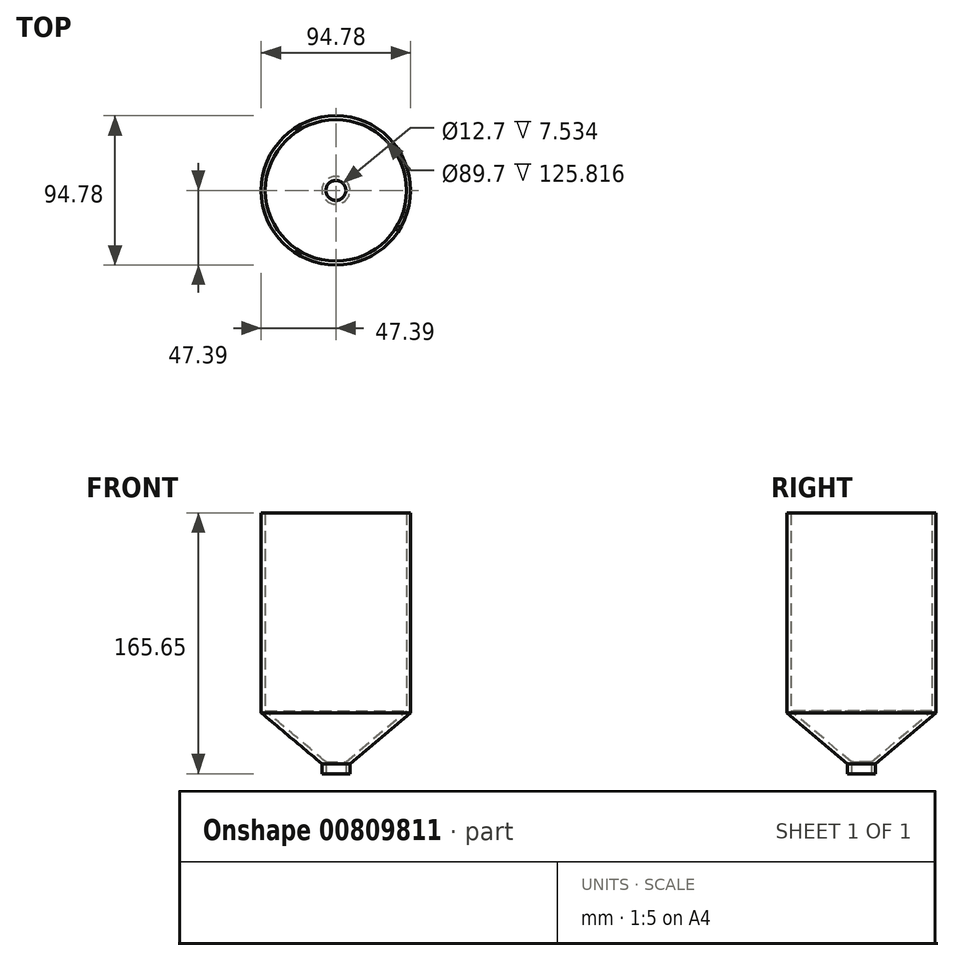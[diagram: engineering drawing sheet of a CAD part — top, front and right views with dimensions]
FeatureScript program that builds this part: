
annotation { "Feature Type Name" : "Feature", "Feature Type Description" : "" }
export const myFeature = defineFeature(function(context is Context, id is Id, definition is map)
    precondition{}
    {
        {
            var Q0;
            Q0=qCreatedBy(makeId("Right.planeOp"),FACE);
            var sketch = newSketch(context, id + "F0", { "sketchPlane" : qUnion([Q0])});
            skLineSegment(sketch, "E0", {"start": v(0, 0) * mm, "end": v(0, 23.87) * mm, "construction": true});
            skLineSegment(sketch, "E1", {"start": v(6.35, 0) * mm, "end": v(6.35, 7.53) * mm});
            skLineSegment(sketch, "E2", {"start": v(6.35, 7.53) * mm, "end": v(44.85, 39.84) * mm});
            skLineSegment(sketch, "E3", {"start": v(44.85, 39.84) * mm, "end": v(44.85, 165.65) * mm});
            skLineSegment(sketch, "E4", {"start": v(44.85, 165.65) * mm, "end": v(47.39, 165.65) * mm});
            skLineSegment(sketch, "E5", {"start": v(47.39, 165.65) * mm, "end": v(47.39, 38.65) * mm});
            skLineSegment(sketch, "E6", {"start": v(47.39, 38.65) * mm, "end": v(8.89, 6.35) * mm});
            skLineSegment(sketch, "E7", {"start": v(8.9, 6.35) * mm, "end": v(8.9, 0) * mm});
            skLineSegment(sketch, "E8", {"start": v(8.9, 0) * mm, "end": v(6.35, 0) * mm});
            skLineSegment(sketch, "E9", {"start": v(6.35, 0) * mm, "end": v(0, 0) * mm});
            skSolve(sketch);
        }
        {
            var Q0;
            Q0=qSketchRegion(id+"F0",true);
            var Q1;
            Q1=sQuery(id+"F0.wireOp",EDGE,"E0");
            revolve(context, id + "F1", {"surfaceOperationType" : NewSurfaceOperationType.NEW, "entities" : qUnion([Q0]), "axis" : qUnion([Q1]), "revolveType" : RevolveType.FULL});
        }
    });
